# Revit family: Light_Shelf-Linear-Kawneer-InLighten
name_source: partatom
category: Specialty Equipment
revit_build: Autodesk Revit 2015 (Build: 20140905_0730(x64)
units: mm (PartAtom-declared; Revit-internal decimal feet)

## types (3) — shared parameters
Bracket Material = Aluminum Composite - Kawneer - Bone White
Default Elevation = 4' - 0"
Description = Light Shelf with a Maximum of 22 Anchors
Manufacturer = Kawneer
Model = InLighten
Product Documentation Link = http://www.kawneer.com
Product Page URL = http://www.kawneer.com
Product data url = https://bimobject.com
Trim Finish = Aluminum Composite - Kawneer - Bone White
URL = http://www.kawneer.com

## per-type parameters (varying)
| type | Panel Finish | Panel Type | Type Comments |
| 16mm Multi-Layer-Extruded-Polycarbonate-Sheet  16 mm | Polycarbonate - Kawneer - 16 mm - Ice | Shelf-Kawneer-16mm_Multi-Layer-Extruded-Polycarbonate-Sheet : 16 mm | Light Shelf Multi Layer Extruded Polycarbonate  16 mm with a Maximum of 22 Anchors |
| 4mm Reynobond-ACM Panel  4 mm | Aluminum Composite - Kawneer - Bone White | Shelf-Kawneer-4mm_Reynobond-ACM Panel : 4 mm | Light Shelf 4mm Reynobond ACM Panel with a Maximum of 22 Anchors |
| 4mm Monolithic-Polycarbonate-Sheet  4 mm | Polycarbonate - Kawneer - 4 mm - Ice | Shelf-Kawneer-4mm_Monolithic-Polycarbonate-Sheet : 4 mm | Light Shelf 4mm Monolithic Polycarbonate with a Maximum of 22 Anchors |

## geometry (parser evidence)
native form markers: Sweep x10
no freeform markers — native parametric forms only
